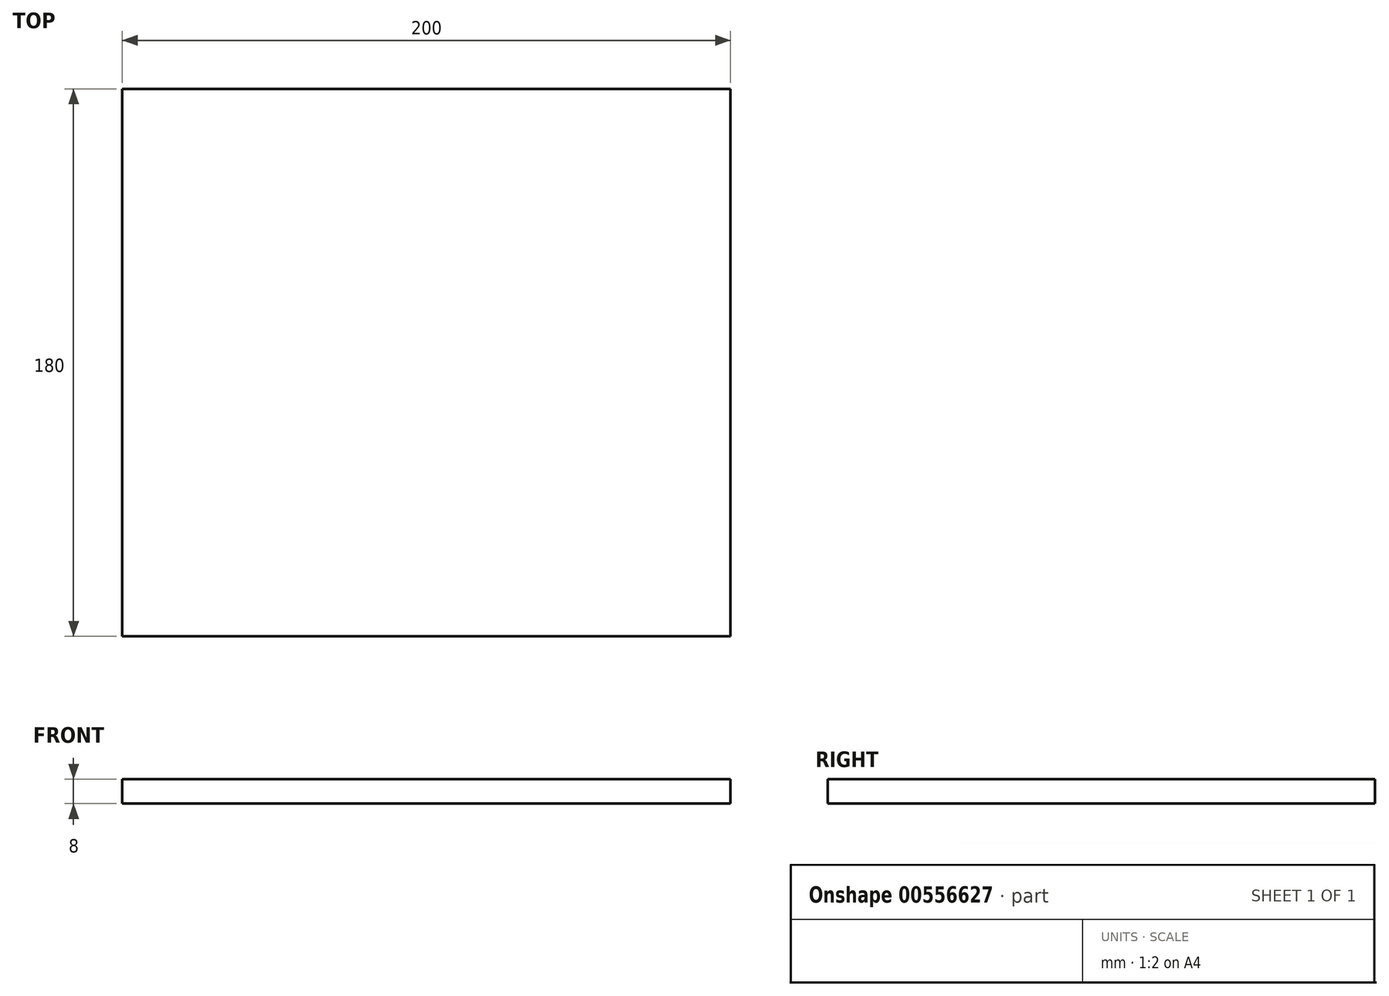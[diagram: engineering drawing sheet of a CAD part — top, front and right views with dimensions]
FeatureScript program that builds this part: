
annotation { "Feature Type Name" : "Feature", "Feature Type Description" : "" }
export const myFeature = defineFeature(function(context is Context, id is Id, definition is map)
    precondition{}
    {
        {
            var Q0;
            Q0=qCreatedBy(makeId("Top.planeOp"),FACE);
            var sketch = newSketch(context, id + "F0", { "sketchPlane" : qUnion([Q0])});
            skLineSegment(sketch, "E0", {"start": v(0, 0) * mm, "end": v(0, -180) * mm});
            skLineSegment(sketch, "E1", {"start": v(0, -180) * mm, "end": v(200, -180) * mm});
            skLineSegment(sketch, "E2", {"start": v(200, -180) * mm, "end": v(200, 0) * mm});
            skLineSegment(sketch, "E3", {"start": v(200, 0) * mm, "end": v(0, 0) * mm});
            skSolve(sketch);
        }
        {
            var Q0;
            Q0=makeQuery(id+"F0.imprint","IMPRINT",FACE,{"disambiguationData":[TD([[makeQuery(id+"F0.imprint","IMPRINT",EDGE,{"derivedFrom":sQuery(id+"F0.wireOp",EDGE,"E0")}),1.0]])]});
            extrude(context, id + "F1", {"entities" : qUnion([Q0]), "depth" : 8 * mm, "offsetDistance" : 25 * mm});
        }
    });
